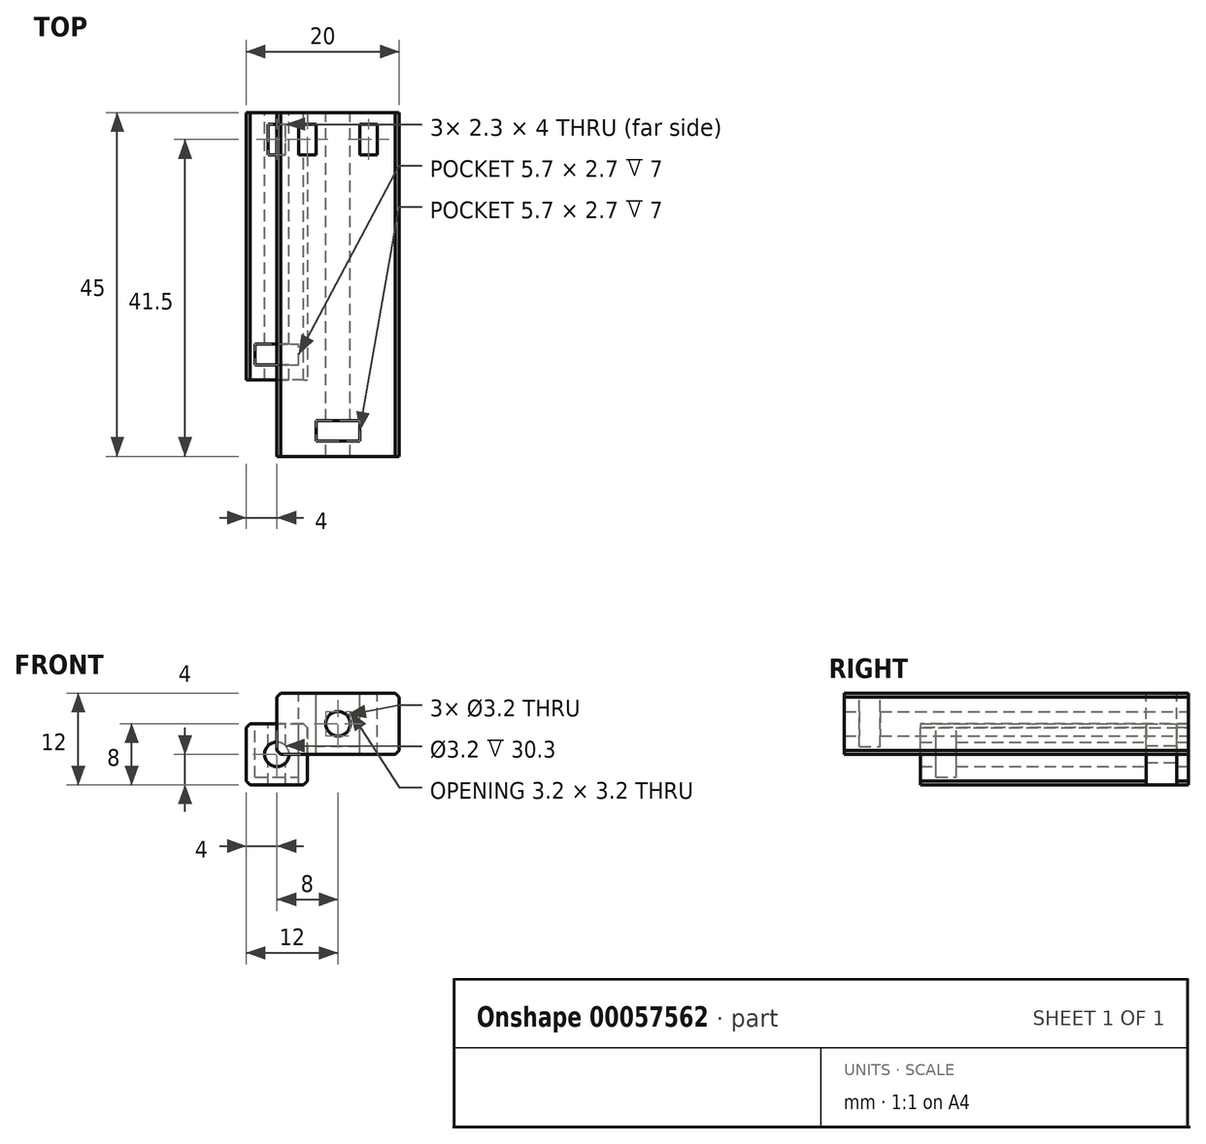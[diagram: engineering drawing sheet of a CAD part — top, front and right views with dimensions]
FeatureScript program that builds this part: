
annotation { "Feature Type Name" : "Feature", "Feature Type Description" : "" }
export const myFeature = defineFeature(function(context is Context, id is Id, definition is map)
    precondition{}
    {
        {
            var Q0;
            Q0=qCreatedBy(makeId("Front.planeOp"),FACE);
            var sketch = newSketch(context, id + "F0", { "sketchPlane" : qUnion([Q0])});
            skLineSegment(sketch, "E0.bottom", {"start": v(4, -4) * mm, "end": v(-4, -4) * mm});
            skLineSegment(sketch, "E0.top", {"start": v(4, 4) * mm, "end": v(-4, 4) * mm});
            skLineSegment(sketch, "E0.left", {"start": v(4, -4) * mm, "end": v(4, 4) * mm});
            skLineSegment(sketch, "E0.right", {"start": v(-4, -4) * mm, "end": v(-4, 4) * mm});
            skPoint(sketch, "E0.middle", {"position": v(0, 0) * mm});
            skCircle(sketch, "E1", {"center": v(0, 0) * mm, "radius": 1.6 * mm});
            skSolve(sketch);
        }
        {
            var Q0;
            Q0=makeQuery(id+"F0.imprint","IMPRINT",FACE,{"disambiguationData":[TD([[makeQuery(id+"F0.imprint","IMPRINT",EDGE,{"derivedFrom":sQuery(id+"F0.wireOp",EDGE,"E0.bottom")}),-1.0]])]});
            extrude(context, id + "F1", {"entities" : qUnion([Q0]), "depth" : 35 * mm});
        }
        {
            var Q0;
            Q0=makeQuery(id+"F1.opExtrude","SWEPT_FACE",FACE,{"disambiguationData":[OSD([sQuery(id+"F0.wireOp",EDGE,"E0.top")])]});
            var sketch = newSketch(context, id + "F2", { "sketchPlane" : qUnion([Q0])});
            skLineSegment(sketch, "E2.bottom", {"start": v(-2.85, -33) * mm, "end": v(2.85, -33) * mm});
            skLineSegment(sketch, "E2.top", {"start": v(-2.85, -30.3) * mm, "end": v(2.85, -30.3) * mm});
            skLineSegment(sketch, "E2.left", {"start": v(-2.85, -33) * mm, "end": v(-2.85, -30.3) * mm});
            skLineSegment(sketch, "E2.right", {"start": v(2.85, -33) * mm, "end": v(2.85, -30.3) * mm});
            skPoint(sketch, "E2.middle", {"position": v(0, -31.65) * mm});
            skSolve(sketch);
        }
        {
            var Q0;
            Q0=makeQuery(id+"F2.imprint","IMPRINT",FACE,{"disambiguationData":[TD([[makeQuery(id+"F2.imprint","IMPRINT",EDGE,{"derivedFrom":sQuery(id+"F2.wireOp",EDGE,"E2.bottom")}),1.0]])]});
            extrude(context, id + "F3", {"entities" : qUnion([Q0]), "operationType" : NewBodyOperationType.REMOVE, "oppositeDirection" : true, "depth" : 7 * mm});
        }
        {
            var Q0;
            Q0=makeQuery(id+"F1.opExtrude","SWEPT_FACE",FACE,{"disambiguationData":[OSD([sQuery(id+"F0.wireOp",EDGE,"E0.top")])]});
            var sketch = newSketch(context, id + "F4", { "sketchPlane" : qUnion([Q0])});
            skLineSegment(sketch, "E3.bottom", {"start": v(-1.15, -5.5) * mm, "end": v(1.15, -5.5) * mm});
            skLineSegment(sketch, "E3.top", {"start": v(-1.15, -1.5) * mm, "end": v(1.15, -1.5) * mm});
            skLineSegment(sketch, "E3.left", {"start": v(-1.15, -5.5) * mm, "end": v(-1.15, -1.5) * mm});
            skLineSegment(sketch, "E3.right", {"start": v(1.15, -5.5) * mm, "end": v(1.15, -1.5) * mm});
            skPoint(sketch, "E3.middle", {"position": v(0, -3.5) * mm});
            skSolve(sketch);
        }
        {
            var Q0;
            Q0=makeQuery(id+"F4.imprint","IMPRINT",FACE,{"disambiguationData":[TD([[makeQuery(id+"F4.imprint","IMPRINT",EDGE,{"derivedFrom":sQuery(id+"F4.wireOp",EDGE,"E3.bottom")}),1.0]])]});
            extrude(context, id + "F5", {"entities" : qUnion([Q0]), "operationType" : NewBodyOperationType.REMOVE, "endBound" : BoundingType.THROUGH_ALL, "oppositeDirection" : true, "depth" : 25 * mm});
        }
        {
            var Q0;
            Q0=makeQuery(id+"F1.opExtrude","SWEPT_EDGE",EDGE,{"disambiguationData":[OSD([sQuery(id+"F0.wireOp",EDGE,"E0.top"),sQuery(id+"F0.wireOp",EDGE,"E0.right")])]});
            var Q1;
            Q1=makeQuery(id+"F1.opExtrude","SWEPT_EDGE",EDGE,{"disambiguationData":[OSD([sQuery(id+"F0.wireOp",EDGE,"E0.top"),sQuery(id+"F0.wireOp",EDGE,"E0.left")])]});
            var Q2;
            Q2=makeQuery(id+"F1.opExtrude","SWEPT_EDGE",EDGE,{"disambiguationData":[OSD([sQuery(id+"F0.wireOp",EDGE,"E0.bottom"),sQuery(id+"F0.wireOp",EDGE,"E0.right")])]});
            var Q3;
            Q3=makeQuery(id+"F1.opExtrude","SWEPT_EDGE",EDGE,{"disambiguationData":[OSD([sQuery(id+"F0.wireOp",EDGE,"E0.bottom"),sQuery(id+"F0.wireOp",EDGE,"E0.left")])]});
            chamfer(context, id + "F6", {"entities" : qUnion([Q0, Q1, Q2, Q3]), "width" : .5 * mm, "tangentPropagation" : true});
        }
        {
            var Q0;
            Q0=qCreatedBy(makeId("Front.planeOp"),FACE);
            var sketch = newSketch(context, id + "F7", { "sketchPlane" : qUnion([Q0])});
            skLineSegment(sketch, "E4.bottom", {"start": v(0, 0) * mm, "end": v(16, 0) * mm});
            skLineSegment(sketch, "E4.top", {"start": v(0, 8) * mm, "end": v(16, 8) * mm});
            skLineSegment(sketch, "E4.left", {"start": v(0, 0) * mm, "end": v(0, 8) * mm});
            skLineSegment(sketch, "E4.right", {"start": v(16, 0) * mm, "end": v(16, 8) * mm});
            skCircle(sketch, "E5", {"center": v(8, 4) * mm, "radius": 1.6 * mm});
            skPoint(sketch, "E5.centerSnap0", {"position": v(8, 8) * mm});
            skLineSegment(sketch, "E6", {"start": v(0, 4) * mm, "end": v(16, 4) * mm, "construction": true});
            skSolve(sketch);
        }
        {
            var Q0;
            Q0=makeQuery(id+"F7.imprint","IMPRINT",FACE,{"disambiguationData":[TD([[makeQuery(id+"F7.imprint","IMPRINT",EDGE,{"derivedFrom":sQuery(id+"F7.wireOp",EDGE,"E4.bottom")}),1.0]])]});
            extrude(context, id + "F8", {"entities" : qUnion([Q0]), "depth" : 45 * mm});
        }
        {
            var Q0;
            Q0=makeQuery(id+"F8.opExtrude","SWEPT_FACE",FACE,{"disambiguationData":[OSD([sQuery(id+"F7.wireOp",EDGE,"E4.top")])]});
            var sketch = newSketch(context, id + "F9", { "sketchPlane" : qUnion([Q0])});
            skLineSegment(sketch, "E7.bottom", {"start": v(10.85, -43) * mm, "end": v(5.15, -43) * mm});
            skLineSegment(sketch, "E7.top", {"start": v(10.85, -40.3) * mm, "end": v(5.15, -40.3) * mm});
            skLineSegment(sketch, "E7.left", {"start": v(10.85, -43) * mm, "end": v(10.85, -40.3) * mm});
            skLineSegment(sketch, "E7.right", {"start": v(5.15, -43) * mm, "end": v(5.15, -40.3) * mm});
            skPoint(sketch, "E7.middle", {"position": v(8, -41.65) * mm});
            skPoint(sketch, "E7.middle.positionSnap0", {"position": v(8, -45) * mm});
            skPoint(sketch, "E7.centerSnap0", {"position": v(8, -45) * mm});
            skSolve(sketch);
        }
        {
            var Q0;
            Q0 = qSketchRegion(id + "F9", true);
            extrude(context, id + "F10", {"entities" : qUnion([Q0]), "operationType" : NewBodyOperationType.REMOVE, "oppositeDirection" : true, "depth" : 7 * mm});
        }
        {
            var Q0;
            Q0=makeQuery(id+"F8.opExtrude","SWEPT_EDGE",EDGE,{"disambiguationData":[OSD([sQuery(id+"F7.wireOp",EDGE,"E4.top"),sQuery(id+"F7.wireOp",EDGE,"E4.left")])]});
            var Q1;
            Q1=makeQuery(id+"F8.opExtrude","SWEPT_EDGE",EDGE,{"disambiguationData":[OSD([sQuery(id+"F7.wireOp",EDGE,"E4.top"),sQuery(id+"F7.wireOp",EDGE,"E4.right")])]});
            var Q2;
            Q2=makeQuery(id+"F8.opExtrude","SWEPT_EDGE",EDGE,{"disambiguationData":[OSD([sQuery(id+"F7.wireOp",EDGE,"E4.bottom"),sQuery(id+"F7.wireOp",EDGE,"E4.right")])]});
            var Q3;
            Q3=makeQuery(id+"F8.opExtrude","SWEPT_EDGE",EDGE,{"disambiguationData":[OSD([sQuery(id+"F7.wireOp",EDGE,"E4.bottom"),sQuery(id+"F7.wireOp",EDGE,"E4.left")])]});
            chamfer(context, id + "F11", {"entities" : qUnion([Q0, Q1, Q2, Q3]), "width" : 0.5 * mm, "tangentPropagation" : true});
        }
        {
            var Q0;
            Q0=makeQuery(id+"F8.opExtrude","SWEPT_FACE",FACE,{"disambiguationData":[OSD([sQuery(id+"F7.wireOp",EDGE,"E4.top")])]});
            var sketch = newSketch(context, id + "F12", { "sketchPlane" : qUnion([Q0])});
            skLineSegment(sketch, "E8.bottom", {"start": v(5.15, -5.5) * mm, "end": v(2.85, -5.5) * mm});
            skLineSegment(sketch, "E8.top", {"start": v(5.15, -1.5) * mm, "end": v(2.85, -1.5) * mm});
            skLineSegment(sketch, "E8.left", {"start": v(5.15, -5.5) * mm, "end": v(5.15, -1.5) * mm});
            skLineSegment(sketch, "E8.right", {"start": v(2.85, -5.5) * mm, "end": v(2.85, -1.5) * mm});
            skPoint(sketch, "E8.middle", {"position": v(4, -3.5) * mm});
            skLineSegment(sketch, "E9", {"start": v(8, 0) * mm, "end": v(8, -10.75) * mm, "construction": true});
            skPoint(sketch, "E10.MirrorP", {"position": v(12, -3.5) * mm});
            skLineSegment(sketch, "E11.MirrorCS", {"start": v(13.15, -5.5) * mm, "end": v(13.15, -1.5) * mm});
            skLineSegment(sketch, "E12.MirrorCS", {"start": v(10.85, -5.5) * mm, "end": v(10.85, -1.5) * mm});
            skLineSegment(sketch, "E13.MirrorCS", {"start": v(10.85, -5.5) * mm, "end": v(13.15, -5.5) * mm});
            skLineSegment(sketch, "E14.MirrorCS", {"start": v(10.85, -1.5) * mm, "end": v(13.15, -1.5) * mm});
            skSolve(sketch);
        }
        {
            var Q0;
            Q0 = qSketchRegion(id + "F12", true);
            extrude(context, id + "F13", {"entities" : qUnion([Q0]), "operationType" : NewBodyOperationType.REMOVE, "endBound" : BoundingType.THROUGH_ALL, "oppositeDirection" : true, "depth" : 25 * mm});
        }
    });
